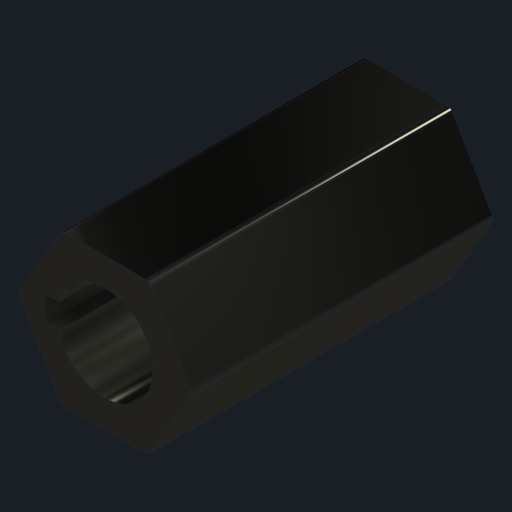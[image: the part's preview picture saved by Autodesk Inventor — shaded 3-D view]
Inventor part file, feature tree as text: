
AUTODESK INVENTOR PART (.ipt)
format: ipt  version: 2024 (Build 280153000, 153)  size: 150,016 bytes
history: native  units: in
note: dims shown in document units (in); Inventor stores cm internally (conversion verified against a paired STEP export)
features: fillet x1
ambient origin geometry x8: Origin, YZ Plane, XZ Plane, XY Plane, X Axis, Y Axis, Z Axis, Center Point
bodies: Solid1 (feature_tree)
feature tree (1):
  fillet  "Fillet1"  [1 undecoded]
note: 1 required parameter value undecoded (feature->parameter linkage not recoverable at this tier; creation-order binding heuristic only, values carry confidence <= 0.55)
